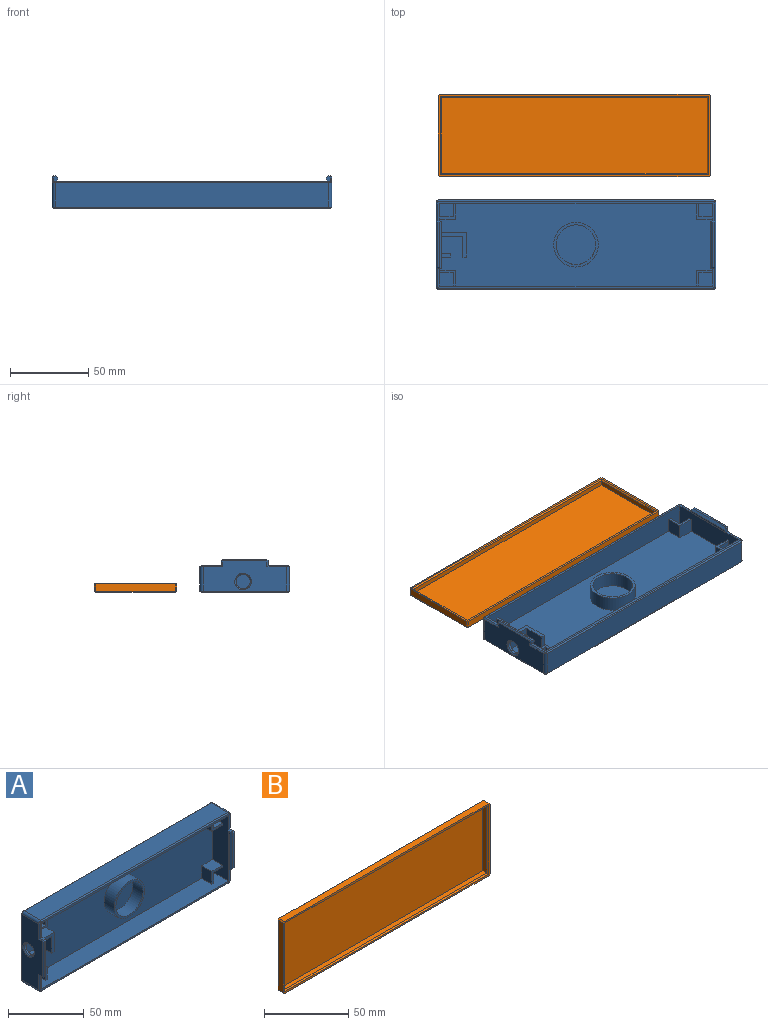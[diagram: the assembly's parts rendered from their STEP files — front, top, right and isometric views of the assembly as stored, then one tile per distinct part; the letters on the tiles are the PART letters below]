
ASSEMBLY  parts=2 mates=1
PART A: 101 faces, bbox 178.4x20.9x57.2 mm
  f0: plane 52.8x14.8mm, normal (-1,0,0), area 743.4mm2, adj f2,f3,f4,f6,f13,f15,f16,f26
  f1: plane 4.5x4.5mm, normal (1,0,0), area 4.3mm2, adj f2,f53,f61
  f2: plane 174x52.8mm, normal (0,-1,0), area 8041.3mm2, adj f0,f1,f4,f13,f14,f18,f22,f23
  f3: plane 8.6x8.6mm, normal (0,-1,0), area 74mm2, adj f0,f4,f36,f39
  f4: plane 174x14.8mm, normal (0,0,1), area 2545.1mm2, adj f0,f2,f3,f5,f14,f16,f32,f33
  f5: plane 8.6x8.6mm, normal (0,-1,0), area 74mm2, adj f4,f14,f31,f32
  f6: plane 8.6x8.6mm, normal (0,-1,0), area 74mm2, adj f0,f13,f26,f27
  f7: plane 8.6x8.6mm, normal (0,-1,0), area 74mm2, adj f13,f14,f21,f24
  f8: plane 53.2x19.3mm, normal (1,0,0), area 935mm2, adj f41,f44,f78,f80,f85,f90,f91,f93
  f9: plane 174.4x15.6mm, normal (0,0,1), area 2720.6mm2, adj f41,f42,f87,f94
  f10: plane 53.2x19.3mm, normal (-1,0,0), area 846.8mm2, adj f42,f43,f68,f70,f75,f79,f82,f98
  f11: plane 174.4x15.6mm, normal (0,0,-1), area 2720.6mm2, adj f43,f44,f73,f97
  f12: plane 176.8x55.6mm, normal (0,1,0), area 9828.8mm2, adj f92,f93,f94,f95,f96,f97,f98,f99
  f13: plane 174x14.8mm, normal (0,0,-1), area 2545.1mm2, adj f0,f2,f6,f7,f14,f15,f23,f24
  f14: plane 52.8x14.8mm, normal (1,0,0), area 632.2mm2, adj f2,f4,f5,f7,f13,f15,f16,f21
  f15: plane 176.8x12.8mm, normal (0,-1,0), area 278.8mm2, adj f0,f13,f14,f45,f48,f82,f84,f87
  f16: plane 176.8x12.8mm, normal (0,-1,0), area 278.8mm2, adj f0,f4,f14,f46,f49,f68,f71,f73
  f17: cylinder r=12.65mm len=25.3mm, axis (0,1,0), area 747.1mm2, adj f19,f20
  f18: cylinder r=14.25mm len=28.5mm, axis (0,1,0), area 841.6mm2, adj f2,f19
  f19: plane 28.5x28.5mm, normal (0,-1,0), area 135.2mm2, adj f17,f18
  f20: plane 25.3x25.3mm, normal (0,-1,0), area 502.7mm2, adj f17
  f21: plane 9.4x8.6mm, normal (0,0,1), area 80.8mm2, adj f7,f14,f24,f25
  f22: plane 10.2x9.4mm, normal (0,0,-1), area 95.9mm2, adj f2,f14,f23,f25
  f23: plane 10.2x9.4mm, normal (1,0,0), area 95.9mm2, adj f2,f13,f22,f25
  f24: plane 9.4x8.6mm, normal (-1,0,0), area 80.8mm2, adj f7,f13,f21,f25
  f25: plane 10.2x10.2mm, normal (0,-1,0), area 30.1mm2, adj f13,f14,f21,f22,f23,f24
  f26: plane 9.4x8.6mm, normal (0,0,1), area 80.8mm2, adj f0,f6,f27,f30
  f27: plane 9.4x8.6mm, normal (1,0,0), area 80.8mm2, adj f6,f13,f26,f30
  f28: plane 10.2x9.4mm, normal (-1,0,0), area 95.9mm2, adj f2,f13,f29,f30
  f29: plane 10.2x9.4mm, normal (0,0,-1), area 95.9mm2, adj f0,f2,f28,f30
  f30: plane 10.2x10.2mm, normal (0,-1,0), area 30.1mm2, adj f0,f13,f26,f27,f28,f29
  f31: plane 9.4x8.6mm, normal (0,0,-1), area 80.8mm2, adj f5,f14,f32,f35
  f32: plane 9.4x8.6mm, normal (-1,0,0), area 80.8mm2, adj f4,f5,f31,f35
  f33: plane 10.2x9.4mm, normal (1,0,0), area 95.9mm2, adj f2,f4,f34,f35
  f34: plane 10.2x9.4mm, normal (0,0,1), area 95.9mm2, adj f2,f14,f33,f35
  f35: plane 10.2x10.2mm, normal (0,-1,0), area 30.1mm2, adj f4,f14,f31,f32,f33,f34
  f36: plane 9.4x8.6mm, normal (0,0,-1), area 80.8mm2, adj f0,f3,f39,f40
  f37: plane 10.2x9.4mm, normal (0,0,1), area 95.9mm2, adj f0,f2,f38,f40
  f38: plane 10.2x9.4mm, normal (-1,0,0), area 95.9mm2, adj f2,f4,f37,f40
  f39: plane 9.4x8.6mm, normal (1,0,0), area 80.8mm2, adj f3,f4,f36,f40
  f40: plane 10.2x10.2mm, normal (0,-1,0), area 30.1mm2, adj f0,f4,f36,f37,f38,f39
  f41: cylinder r=2mm len=15.6mm, axis (0,1,0), area 49mm2, adj f8,f9,f89,f92
  f42: cylinder r=2mm len=15.6mm, axis (0,1,0), area 49mm2, adj f9,f10,f84,f96
  f43: cylinder r=2mm len=15.6mm, axis (0,-1,0), area 49mm2, adj f10,f11,f71,f99
  f44: cylinder r=2mm len=15.6mm, axis (0,-1,0), area 49mm2, adj f8,f11,f76,f95
  f45: plane 3.17x2.6mm, normal (0,0,1), area 6.9mm2, adj f14,f15,f62,f64,f65,f74,f79
  f46: plane 3.17x2.6mm, normal (0,0,-1), area 6.9mm2, adj f14,f16,f62,f64,f65,f69,f70
  f47: plane 28.4x1.1mm, normal (0,-1,0), area 31.2mm2, adj f65,f69,f74,f75
  f48: plane 3.17x2.6mm, normal (0,0,1), area 6.9mm2, adj f0,f15,f63,f66,f67,f86,f90
  f49: plane 3.17x2.6mm, normal (0,0,-1), area 6.9mm2, adj f0,f16,f63,f66,f67,f80,f81
  f50: plane 28.4x1.1mm, normal (0,-1,0), area 31.2mm2, adj f67,f81,f85,f86
  f51: plane 15.8x9mm, normal (1,0,0), area 142.2mm2, adj f2,f52,f55,f56
  f52: plane 17.29x9mm, normal (0,0,1), area 155.6mm2, adj f2,f14,f51,f56
  f53: plane 14.89x9mm, normal (0,0,-1), area 133.1mm2, adj f1,f2,f14,f54,f56,f61
  f54: plane 13.4x9mm, normal (-1,0,0), area 120.6mm2, adj f2,f53,f55,f56
  f55: plane 9x2.4mm, normal (0,0,-1), area 21.6mm2, adj f2,f51,f54,f56
  f56: plane 17.29x15.8mm, normal (0,-1,0), area 73.7mm2, adj f14,f51,f52,f53,f54,f55
  f57: plane 9x7.2mm, normal (0,0,1), area 64.8mm2, adj f2,f14,f59,f60
  f58: plane 9x7.2mm, normal (0,0,-1), area 64.8mm2, adj f2,f14,f59,f60
  f59: plane 9x2.4mm, normal (1,0,0), area 21.6mm2, adj f2,f57,f58,f60
  f60: plane 7.2x2.4mm, normal (0,-1,0), area 17.3mm2, adj f14,f57,f58,f59
  f61: cylinder r=4.5mm len=9mm, axis (1,0,0), area 41mm2, adj f1,f2,f14,f53,f100
  f62: plane 30x1.27mm, normal (1,0,0), area 38mm2, adj f45,f46,f64,f65
  f63: plane 30x1.27mm, normal (-1,0,0), area 38mm2, adj f48,f49,f66,f67
  f64: plane 30x1.2mm, normal (0.71,0.71,0), area 50.9mm2, adj f14,f45,f46,f62
  f65: plane 30x1.5mm, normal (0.71,-0.71,0), area 62.7mm2, adj f45,f46,f47,f62,f69,f74
  f66: plane 30x1.2mm, normal (-0.71,0.71,0), area 50.9mm2, adj f0,f48,f49,f63
  f67: plane 30x1.5mm, normal (-0.71,-0.71,0), area 62.7mm2, adj f48,f49,f50,f63,f81,f86
  f68: plane 12.4x0.8mm, normal (-0.71,-0.71,0), area 13.6mm2, adj f10,f16,f70,f71
  f69: plane 1.9x0.8mm, normal (0,-0.71,-0.71), area 1.7mm2, adj f46,f47,f65,f72
  f70: plane 3.7x0.8mm, normal (-0.71,0,-0.71), area 3.7mm2, adj f10,f46,f68,f72
  f71: cone r=1.2mm half-angle=45deg, axis (0,1,0), area 2.8mm2, adj f16,f43,f68,f73
  f72: plane 0.8x0.8mm, normal (-0.58,-0.58,-0.58), area 0.6mm2, adj f69,f70,f75
  f73: plane 174.4x0.8mm, normal (0,-0.71,-0.71), area 197.3mm2, adj f11,f16,f71,f76
  f74: plane 1.9x0.8mm, normal (0,-0.71,0.71), area 1.7mm2, adj f45,f47,f65,f77
  f75: plane 28.4x0.8mm, normal (-0.71,-0.71,0), area 32.1mm2, adj f10,f47,f72,f77
  f76: cone r=1.2mm half-angle=45deg, axis (0,1,0), area 2.8mm2, adj f16,f44,f73,f78
  f77: plane 0.8x0.8mm, normal (-0.58,-0.58,0.58), area 0.6mm2, adj f74,f75,f79
  f78: plane 12.4x0.8mm, normal (0.71,-0.71,0), area 13.6mm2, adj f8,f16,f76,f80
  f79: plane 3.7x0.8mm, normal (-0.71,0,0.71), area 3.7mm2, adj f10,f45,f77,f82
  f80: plane 3.7x0.8mm, normal (0.71,0,-0.71), area 3.7mm2, adj f8,f49,f78,f83
  f81: plane 1.9x0.8mm, normal (0,-0.71,-0.71), area 1.7mm2, adj f49,f50,f67,f83
  f82: plane 12.4x0.8mm, normal (-0.71,-0.71,0), area 13.6mm2, adj f10,f15,f79,f84
  f83: plane 0.8x0.8mm, normal (0.58,-0.58,-0.58), area 0.6mm2, adj f80,f81,f85
  f84: cone r=1.2mm half-angle=45deg, axis (0,1,0), area 2.8mm2, adj f15,f42,f82,f87
  f85: plane 28.4x0.8mm, normal (0.71,-0.71,0), area 32.1mm2, adj f8,f50,f83,f88
  f86: plane 1.9x0.8mm, normal (0,-0.71,0.71), area 1.7mm2, adj f48,f50,f67,f88
  f87: plane 174.4x0.8mm, normal (0,-0.71,0.71), area 197.3mm2, adj f9,f15,f84,f89
  f88: plane 0.8x0.8mm, normal (0.58,-0.58,0.58), area 0.6mm2, adj f85,f86,f90
  f89: cone r=1.2mm half-angle=45deg, axis (0,1,0), area 2.8mm2, adj f15,f41,f87,f91
  f90: plane 3.7x0.8mm, normal (0.71,0,0.71), area 3.7mm2, adj f8,f48,f88,f91
  f91: plane 12.4x0.8mm, normal (0.71,-0.71,0), area 13.6mm2, adj f8,f15,f89,f90
  f92: cone r=1.2mm half-angle=45deg, axis (0,-1,0), area 2.8mm2, adj f12,f41,f93,f94
  f93: plane 53.2x0.8mm, normal (0.71,0.71,0), area 60.2mm2, adj f8,f12,f92,f95
  f94: plane 174.4x0.8mm, normal (0,0.71,0.71), area 197.3mm2, adj f9,f12,f92,f96
  f95: cone r=1.2mm half-angle=45deg, axis (0,-1,0), area 2.8mm2, adj f12,f44,f93,f97
  f96: cone r=1.2mm half-angle=45deg, axis (0,-1,0), area 2.8mm2, adj f12,f42,f94,f98
  f97: plane 174.4x0.8mm, normal (0,0.71,-0.71), area 197.3mm2, adj f11,f12,f95,f99
  f98: plane 53.2x0.8mm, normal (-0.71,0.71,0), area 60.2mm2, adj f10,f12,f96,f99
  f99: cone r=1.2mm half-angle=45deg, axis (0,-1,0), area 2.8mm2, adj f12,f43,f97,f98
  f100: cone r=4.5mm half-angle=45deg, axis (-1,0,0), area 34.8mm2, adj f10,f61
PART B: 27 faces, bbox 173.6x5.4x52.4 mm
  f0: plane 50.8x4.6mm, normal (1,0,0), area 233.7mm2, adj f9,f11,f12,f13
  f1: plane 172x4.6mm, normal (0,0,1), area 791.2mm2, adj f9,f11,f16,f17
  f2: plane 50.8x4.6mm, normal (-1,0,0), area 233.7mm2, adj f9,f17,f18,f22
  f3: plane 172x4.6mm, normal (0,0,-1), area 791.2mm2, adj f9,f12,f18,f19
  f4: plane 172x50.8mm, normal (0,1,0), area 8737.6mm2, adj f13,f16,f19,f22
  f5: plane 169.6x3.2mm, normal (0,0,-1), area 542.7mm2, adj f6,f8,f10,f24
  f6: plane 48.4x3.2mm, normal (-1,0,0), area 154.9mm2, adj f5,f7,f10,f26
  f7: plane 169.6x3.2mm, normal (0,0,1), area 542.7mm2, adj f6,f8,f10,f25
  f8: plane 48.4x3.2mm, normal (1,0,0), area 154.9mm2, adj f5,f7,f10,f23
  f9: plane 173.6x52.4mm, normal (0,-1,0), area 535.4mm2, adj f0,f1,f2,f3,f11,f12,f17,f18
  f10: plane 169.6x48.4mm, normal (0,-1,0), area 8208.6mm2, adj f5,f6,f7,f8
  f11: plane 4.6x0.8mm, normal (0.71,0,0.71), area 5.2mm2, adj f0,f1,f9,f14
  f12: plane 4.6x0.8mm, normal (0.71,0,-0.71), area 5.2mm2, adj f0,f3,f9,f15
  f13: plane 50.8x0.8mm, normal (0.71,0.71,0), area 57.5mm2, adj f0,f4,f14,f15
  f14: plane 0.8x0.8mm, normal (0.58,0.58,0.58), area 0.6mm2, adj f11,f13,f16
  f15: plane 0.8x0.8mm, normal (0.58,0.58,-0.58), area 0.6mm2, adj f12,f13,f19
  f16: plane 172x0.8mm, normal (0,0.71,0.71), area 194.6mm2, adj f1,f4,f14,f20
  f17: plane 4.6x0.8mm, normal (-0.71,0,0.71), area 5.2mm2, adj f1,f2,f9,f20
  f18: plane 4.6x0.8mm, normal (-0.71,0,-0.71), area 5.2mm2, adj f2,f3,f9,f21
  f19: plane 172x0.8mm, normal (0,0.71,-0.71), area 194.6mm2, adj f3,f4,f15,f21
  f20: plane 0.8x0.8mm, normal (-0.58,0.58,0.58), area 0.6mm2, adj f16,f17,f22
  f21: plane 0.8x0.8mm, normal (-0.58,0.58,-0.58), area 0.6mm2, adj f18,f19,f22
  f22: plane 50.8x0.8mm, normal (-0.71,0.71,0), area 57.5mm2, adj f2,f4,f20,f21
  f23: plane 50x0.8mm, normal (0.71,-0.71,0), area 55.7mm2, adj f8,f9,f24,f25
  f24: plane 171.2x0.8mm, normal (0,-0.71,-0.71), area 192.8mm2, adj f5,f9,f23,f26
  f25: plane 171.2x0.8mm, normal (0,-0.71,0.71), area 192.8mm2, adj f7,f9,f23,f26
  f26: plane 50x0.8mm, normal (-0.71,-0.71,0), area 55.7mm2, adj f6,f9,f24,f25
PLACE A rot(axis=(-1,0,0),90deg) t=(1.04,-56.37,179.18)mm
PLACE B rot(axis=(-1,0,0),90deg) t=(-0.06,13.3,148.18)mm
MATE planar B.f4 <-> A.f17  axis (0,0,-1) through (-0.06,32.3,56.78)mm
